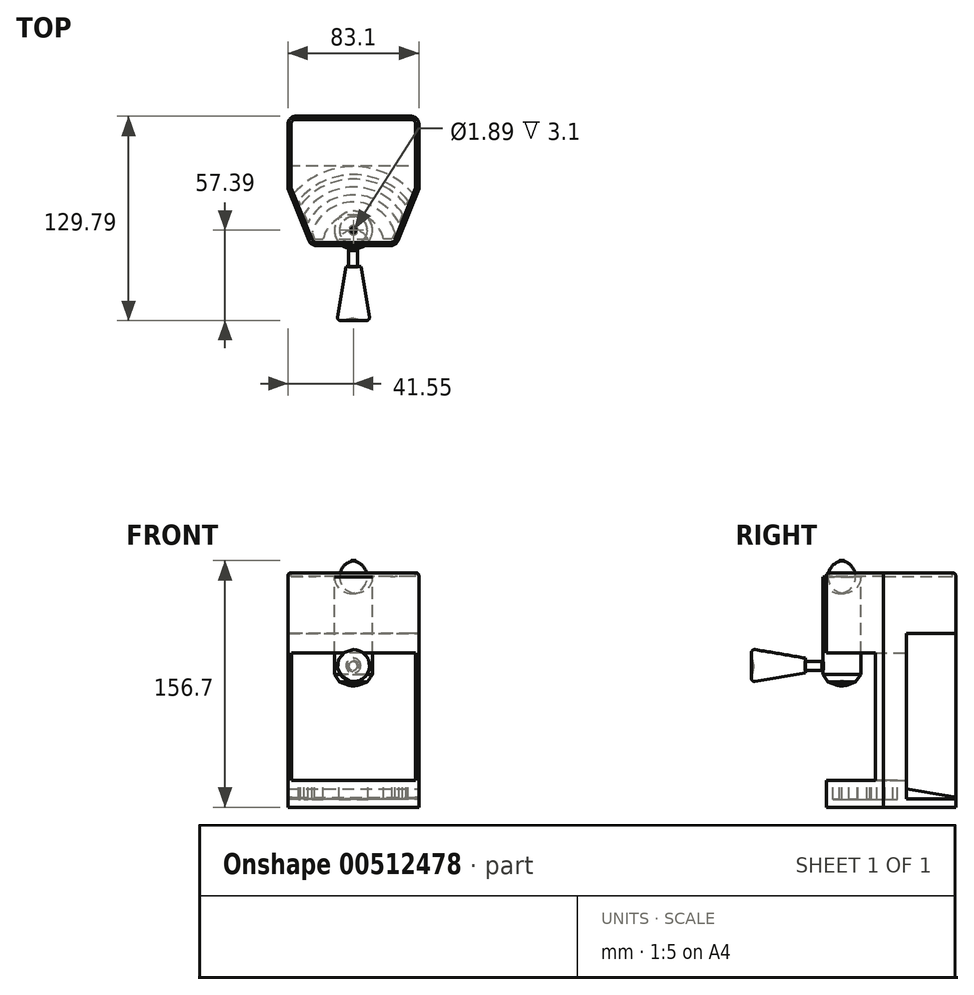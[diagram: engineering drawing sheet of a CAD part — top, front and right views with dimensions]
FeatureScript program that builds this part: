
annotation { "Feature Type Name" : "Feature", "Feature Type Description" : "" }
export const myFeature = defineFeature(function(context is Context, id is Id, definition is map)
    precondition{}
    {
        {
            var Q0;
            Q0=qCreatedBy(makeId("Top.planeOp"),FACE);
            var sketch = newSketch(context, id + "F0", { "sketchPlane" : qUnion([Q0])});
            skLineSegment(sketch, "E0.bottom", {"start": v(23.61, -41.08) * mm, "end": v(-23.61, -41.08) * mm});
            skLineSegment(sketch, "E0.top", {"start": v(36.55, 41.08) * mm, "end": v(-36.55, 41.08) * mm});
            skLineSegment(sketch, "E0.left", {"start": v(41.55, -4.86) * mm, "end": v(41.55, 36.08) * mm});
            skLineSegment(sketch, "E0.right", {"start": v(-41.55, -4.86) * mm, "end": v(-41.55, 36.08) * mm});
            skPoint(sketch, "E0.middle", {"position": v(0, 0) * mm});
            skLineSegment(sketch, "E1", {"start": v(-41.55, -4.86) * mm, "end": v(-28.25, -37.94) * mm});
            skPoint(sketch, "E2.orphan", {"position": v(-41.55, -41.08) * mm});
            skLineSegment(sketch, "E3.MirrorCS", {"start": v(41.55, -4.86) * mm, "end": v(28.25, -37.94) * mm});
            skPoint(sketch, "E4.orphan", {"position": v(41.55, -41.08) * mm});
            skPoint(sketch, "E5.orphan", {"position": v(-50.34, 17.01) * mm});
            skPoint(sketch, "E6.start.orphan", {"position": v(-21.47, -54.8) * mm});
            skPoint(sketch, "E7.orphan", {"position": v(21.47, -54.8) * mm});
            skPoint(sketch, "E8.orphan", {"position": v(50.34, 17.01) * mm});
            skPoint(sketch, "E9.visualSharp", {"position": v(-41.55, 41.08) * mm});
            skArc(sketch, "E9.filletArc", {"start": v(-36.55, 41.08) * mm, "mid": v(-40.08, 39.61) * mm, "end": v(-41.55, 36.08) * mm});
            skPoint(sketch, "E10.visualSharp", {"position": v(41.55, 41.08) * mm});
            skArc(sketch, "E10.filletArc", {"start": v(41.55, 36.08) * mm, "mid": v(40.08, 39.61) * mm, "end": v(36.55, 41.08) * mm});
            skPoint(sketch, "E11.visualSharp", {"position": v(-27, -41.08) * mm});
            skArc(sketch, "E11.filletArc", {"start": v(-28.25, -37.94) * mm, "mid": v(-26.41, -40.22) * mm, "end": v(-23.61, -41.08) * mm});
            skPoint(sketch, "E12.visualSharp", {"position": v(27, -41.08) * mm});
            skArc(sketch, "E12.filletArc", {"start": v(23.61, -41.08) * mm, "mid": v(26.41, -40.22) * mm, "end": v(28.25, -37.94) * mm});
            skSolve(sketch);
        }
        {
            var Q0;
            Q0=makeQuery(id+"F0.imprint","IMPRINT",FACE,{"disambiguationData":[TD([[makeQuery(id+"F0.imprint","IMPRINT",EDGE,{"derivedFrom":sQuery(id+"F0.wireOp",EDGE,"E0.bottom")}),-1.0]])]});
            extrude(context, id + "F1", {"entities" : qUnion([Q0]), "depth" : 149 * mm});
        }
        {
            var Q0;
            Q0=qCreatedBy(makeId("Top.planeOp"),FACE);
            cPlane(context, id + "F2", {"entities" : qUnion([Q0]), "cplaneType" : CPlaneType.OFFSET, "offset" : 17 * mm, "width" : 150 * mm, "height" : 150 * mm});
        }
        {
            var Q0;
            Q0=qCreatedBy(id+"F2.planeOp",FACE);
            var sketch = newSketch(context, id + "F3", { "sketchPlane" : qUnion([Q0])});
            skCircle(sketch, "E13", {"center": v(0, -41.15) * mm, "radius": 50.23 * mm});
            skSolve(sketch);
        }
        {
            var Q0;
            Q0=makeQuery(id+"F3.imprint","IMPRINT",FACE,{"disambiguationData":[TD([[makeQuery(id+"F3.imprint","IMPRINT",EDGE,{"derivedFrom":sQuery(id+"F3.wireOp",EDGE,"E13")}),1.0]])]});
            extrude(context, id + "F4", {"entities" : qUnion([Q0]), "operationType" : NewBodyOperationType.REMOVE, "depth" : 81 * mm});
        }
        {
            var Q0;
            Q0=makeQuery(id+"F4.boolean.opBoolean","COPY",FACE,{"derivedFrom":makeQuery(id+"F4.opExtrude","CAP_FACE",FACE,{"disambiguationData":[OSD([sQuery(id+"F3.wireOp",EDGE,"E13")])],"isStart":false})});
            cPlane(context, id + "F5", {"entities" : qUnion([Q0]), "cplaneType" : CPlaneType.OFFSET, "offset" : 0 * mm, "width" : 150 * mm, "height" : 150 * mm});
        }
        {
            var Q0;
            Q0=makeQuery(id+"F1.opExtrude","CAP_FACE",FACE,{"disambiguationData":[OSD([sQuery(id+"F0.wireOp",EDGE,"E0.bottom"),sQuery(id+"F0.wireOp",EDGE,"E0.top"),sQuery(id+"F0.wireOp",EDGE,"E0.left"),sQuery(id+"F0.wireOp",EDGE,"E0.right"),sQuery(id+"F0.wireOp",EDGE,"E1"),sQuery(id+"F0.wireOp",EDGE,"E3.MirrorCS"),sQuery(id+"F0.wireOp",EDGE,"E9.filletArc"),sQuery(id+"F0.wireOp",EDGE,"E10.filletArc"),sQuery(id+"F0.wireOp",EDGE,"E11.filletArc"),sQuery(id+"F0.wireOp",EDGE,"E12.filletArc")])],"isStart":false});
            fillet(context, id + "F6", {"entities" : qUnion([Q0]), "radius" : 2 * mm, "tangentPropagation" : true, "allowEdgeOverflow" : false});
        }
        {
            var Q0;
            Q0=qCreatedBy(id+"F5.planeOp",FACE);
            var sketch = newSketch(context, id + "F7", { "sketchPlane" : qUnion([Q0])});
            skCircle(sketch, "E14", {"center": v(0, 31.32) * mm, "radius": 12.05 * mm});
            skSolve(sketch);
        }
        {
            var Q0;
            Q0=makeQuery(id+"F1.opExtrude","CAP_FACE",FACE,{"disambiguationData":[OSD([sQuery(id+"F0.wireOp",EDGE,"E0.bottom"),sQuery(id+"F0.wireOp",EDGE,"E0.top"),sQuery(id+"F0.wireOp",EDGE,"E0.left"),sQuery(id+"F0.wireOp",EDGE,"E0.right"),sQuery(id+"F0.wireOp",EDGE,"E1"),sQuery(id+"F0.wireOp",EDGE,"E3.MirrorCS"),sQuery(id+"F0.wireOp",EDGE,"E9.filletArc"),sQuery(id+"F0.wireOp",EDGE,"E10.filletArc"),sQuery(id+"F0.wireOp",EDGE,"E11.filletArc"),sQuery(id+"F0.wireOp",EDGE,"E12.filletArc")])],"isStart":false});
            extrude(context, id + "F8", {"entities" : qUnion([Q0]), "operationType" : NewBodyOperationType.REMOVE, "oppositeDirection" : true, "depth" : 2.5 * mm, "offsetDistance" : 25 * mm});
        }
        {
            var Q0;
            Q0=makeQuery(id+"F7.imprint","IMPRINT",FACE,{"disambiguationData":[TD([[makeQuery(id+"F7.imprint","IMPRINT",EDGE,{"derivedFrom":sQuery(id+"F7.wireOp",EDGE,"E14")}),1.0]])]});
            extrude(context, id + "F9", {"entities" : qUnion([Q0]), "depth" : 20.8 * mm, "hasSecondDirection" : true, "secondDirectionOppositeDirection" : true, "secondDirectionDepth" : 58.7 * mm, "offsetDistance" : 25 * mm});
        }
        {
            var Q0;
            Q0=makeQuery(id+"F9.opExtrude","CAP_EDGE",EDGE,{"disambiguationData":[OSD([sQuery(id+"F7.wireOp",EDGE,"E14")])],"isStart":false});
            chamfer(context, id + "F10", {"entities" : qUnion([Q0]), "chamferType" : ChamferType.OFFSET_ANGLE, "width" : 10 * mm, "oppositeDirection" : false, "angle" : 20 * degree, "tangentPropagation" : true});
        }
        {
            var Q0;
            Q0=makeQuery(id+"F4.boolean.opBoolean","COPY",FACE,{"derivedFrom":makeQuery(id+"F4.opExtrude","CAP_FACE",FACE,{"disambiguationData":[OSD([sQuery(id+"F3.wireOp",EDGE,"E13")])],"isStart":true})});
            cPlane(context, id + "F11", {"entities" : qUnion([Q0]), "cplaneType" : CPlaneType.OFFSET, "offset" : 0 * mm, "width" : 150 * mm, "height" : 150 * mm});
        }
        {
            var Q0;
            Q0=qCreatedBy(id+"F11.planeOp",FACE);
            var sketch = newSketch(context, id + "F12", { "sketchPlane" : qUnion([Q0])});
            skArc(sketch, "E15", {"start": v(34.7, -12.42) * mm, "mid": v(0, 3.9) * mm, "end": v(-34.7, -12.42) * mm});
            skArc(sketch, "E16", {"start": v(33.47, -15.42) * mm, "mid": v(0, 1.06) * mm, "end": v(-33.47, -15.42) * mm});
            skArc(sketch, "E17", {"start": v(31.22, -20.93) * mm, "mid": v(0, -3.95) * mm, "end": v(-31.22, -20.93) * mm});
            skArc(sketch, "E18", {"start": v(28.85, -26.71) * mm, "mid": v(0, -8.89) * mm, "end": v(-28.85, -26.71) * mm});
            skArc(sketch, "E19", {"start": v(26.4, -32.73) * mm, "mid": v(0, -13.45) * mm, "end": v(-26.4, -32.73) * mm});
            skArc(sketch, "E20", {"start": v(19.24, -37.09) * mm, "mid": v(0, -21.49) * mm, "end": v(-19.24, -37.09) * mm});
            skArc(sketch, "E21", {"start": v(9.18, -37.09) * mm, "mid": v(0, -31.11) * mm, "end": v(-9.18, -37.09) * mm});
            skLineSegment(sketch, "E22", {"start": v(-34.7, -12.42) * mm, "end": v(-33.47, -15.42) * mm});
            skLineSegment(sketch, "E23", {"start": v(-24.6, -37.09) * mm, "end": v(-19.24, -37.09) * mm});
            skLineSegment(sketch, "E24.MirrorCS", {"start": v(24.6, -37.09) * mm, "end": v(19.24, -37.09) * mm});
            skLineSegment(sketch, "E25.MirrorCS", {"start": v(34.7, -12.42) * mm, "end": v(33.47, -15.42) * mm});
            skPoint(sketch, "E26.orphan", {"position": v(-38.23, -3.78) * mm});
            skPoint(sketch, "E27.orphan", {"position": v(38.23, -3.78) * mm});
            skLineSegment(sketch, "E28.trimOffspring", {"start": v(-31.22, -20.93) * mm, "end": v(-28.85, -26.71) * mm});
            skLineSegment(sketch, "E29.trimOffspring", {"start": v(31.22, -20.93) * mm, "end": v(28.85, -26.71) * mm});
            skLineSegment(sketch, "E30.trimOffspring", {"start": v(26.4, -32.73) * mm, "end": v(24.6, -37.09) * mm});
            skLineSegment(sketch, "E31.trimOffspring", {"start": v(-26.4, -32.73) * mm, "end": v(-24.6, -37.09) * mm});
            skPoint(sketch, "E32.trimOffspring.end.orphan", {"position": v(5.22, -37.09) * mm});
            skPoint(sketch, "E33.trimOffspring.end.orphan", {"position": v(-5.22, -37.09) * mm});
            skLineSegment(sketch, "E34", {"start": v(-9.18, -37.09) * mm, "end": v(9.18, -37.09) * mm});
            skSolve(sketch);
        }
        {
            var Q0;
            Q0=makeQuery(id+"F12.imprint","IMPRINT",FACE,{"disambiguationData":[TD([[makeQuery(id+"F12.imprint","IMPRINT",EDGE,{"derivedFrom":sQuery(id+"F12.wireOp",EDGE,"E19")}),1.0]])]});
            var Q1;
            Q1=makeQuery(id+"F12.imprint","IMPRINT",FACE,{"disambiguationData":[TD([[makeQuery(id+"F12.imprint","IMPRINT",EDGE,{"derivedFrom":sQuery(id+"F12.wireOp",EDGE,"E17")}),1.0]])]});
            var Q2;
            Q2=makeQuery(id+"F12.imprint","IMPRINT",FACE,{"disambiguationData":[TD([[makeQuery(id+"F12.imprint","IMPRINT",EDGE,{"derivedFrom":sQuery(id+"F12.wireOp",EDGE,"E15")}),1.0]])]});
            var Q3;
            Q3=makeQuery(id+"F12.imprint","IMPRINT",FACE,{"disambiguationData":[TD([[makeQuery(id+"F12.imprint","IMPRINT",EDGE,{"derivedFrom":sQuery(id+"F12.wireOp",EDGE,"E21")}),1.0]])]});
            extrude(context, id + "F13", {"entities" : qUnion([Q0, Q1, Q2, Q3]), "operationType" : NewBodyOperationType.REMOVE, "oppositeDirection" : true, "depth" : 11.9 * mm});
        }
        {
            var Q0;
            Q0=makeQuery(id+"F9.opExtrude","CAP_EDGE",EDGE,{"disambiguationData":[OSD([sQuery(id+"F7.wireOp",EDGE,"E14")])],"isStart":true});
            fillet(context, id + "F14", {"entities" : qUnion([Q0]), "radius" : 10.38 * mm, "tangentPropagation" : true, "allowEdgeOverflow" : false});
        }
        {
            var Q0;
            Q0=qCreatedBy(makeId("Right.planeOp"),FACE);
            var sketch = newSketch(context, id + "F15", { "sketchPlane" : qUnion([Q0])});
            skLineSegment(sketch, "E35", {"start": v(50.85, 137.76) * mm, "end": v(50.85, 110.55) * mm});
            skLineSegment(sketch, "E36", {"start": v(50.85, 110.55) * mm, "end": v(9.66, 110.55) * mm});
            skLineSegment(sketch, "E37", {"start": v(9.66, 110.55) * mm, "end": v(9.66, 11.61) * mm});
            skLineSegment(sketch, "E38", {"start": v(9.66, 11.61) * mm, "end": v(46.8, 5.36) * mm});
            skLineSegment(sketch, "E39", {"start": v(46.8, 5.36) * mm, "end": v(79.54, 105.4) * mm});
            skLineSegment(sketch, "E40", {"start": v(79.54, 105.4) * mm, "end": v(50.85, 137.76) * mm});
            skSolve(sketch);
        }
        {
            var Q0;
            Q0=makeQuery(id+"F15.imprint","IMPRINT",FACE,{"disambiguationData":[TD([[makeQuery(id+"F15.imprint","IMPRINT",EDGE,{"derivedFrom":sQuery(id+"F15.wireOp",EDGE,"E35")}),1.0]])]});
            extrude(context, id + "F16", {"entities" : qUnion([Q0]), "operationType" : NewBodyOperationType.REMOVE, "oppositeDirection" : true, "depth" : 88 * mm, "offsetDistance" : 25 * mm, "symmetric" : true});
        }
        {
            var Q0;
            Q0=makeQuery(id+"F16.boolean.opBoolean","COPY",FACE,{"derivedFrom":makeQuery(id+"F16.opExtrude","SWEPT_FACE",FACE,{"disambiguationData":[OSD([sQuery(id+"F15.wireOp",EDGE,"E36")])]})});
            extrude(context, id + "F17", {"entities" : qUnion([Q0]), "depth" : 105.3 * mm, "offsetDistance" : 25 * mm});
        }
        {
            var Q0;
            {var subQ2=sQuery(id+"F0.wireOp",EDGE,"E0.bottom");Q0=makeQuery(id+"F4.boolean.opBoolean","SPLIT",FACE,{"disambiguationData":[TD([makeQuery(id+"F4.opExtrude","CAP_FACE",FACE,{"disambiguationData":[OSD([sQuery(id+"F3.wireOp",EDGE,"E13")])],"isStart":false})])],"derivedFrom":makeQuery(id+"F1.opExtrude","SWEPT_FACE",FACE,{"disambiguationData":[OSD([subQ2])]})});}
            var sketch = newSketch(context, id + "F18", { "sketchPlane" : qUnion([Q0])});
            skCircle(sketch, "E41", {"center": v(-0.2, 89.77) * mm, "radius": 2.75 * mm});
            skSolve(sketch);
        }
        {
            var Q0;
            Q0 = qSketchRegion(id + "F18", true);
            extrude(context, id + "F19", {"entities" : qUnion([Q0]), "operationType" : NewBodyOperationType.ADD, "depth" : 14 * mm, "offsetDistance" : 25 * mm});
        }
        {
            var Q0;
            Q0=qCreatedBy(makeId("Right.planeOp"),FACE);
            var sketch = newSketch(context, id + "F20", { "sketchPlane" : qUnion([Q0])});
            skLineSegment(sketch, "E42", {"start": v(-55, 90.05) * mm, "end": v(-87.25, 90.05) * mm});
            skLineSegment(sketch, "E43", {"start": v(-87.25, 90.05) * mm, "end": v(-88.68, 97.87) * mm});
            skLineSegment(sketch, "E44", {"start": v(-86.37, 100.2) * mm, "end": v(-54.55, 94.74) * mm});
            skLineSegment(sketch, "E45", {"start": v(-54.55, 94.74) * mm, "end": v(-55, 90.05) * mm});
            skPoint(sketch, "E46.visualSharp", {"position": v(-89.19, 100.69) * mm});
            skArc(sketch, "E46.filletArc", {"start": v(-86.37, 100.2) * mm, "mid": v(-88.13, 99.64) * mm, "end": v(-88.68, 97.87) * mm});
            skSolve(sketch);
        }
        {
            var Q0;
            Q0=makeQuery(id+"F20.imprint","IMPRINT",FACE,{"disambiguationData":[TD([[makeQuery(id+"F20.imprint","IMPRINT",EDGE,{"derivedFrom":sQuery(id+"F20.wireOp",EDGE,"E42")}),-1.0]])]});
            var Q1;
            Q1=sQuery(id+"F20.wireOp",EDGE,"E42");
            revolve(context, id + "F21", {"entities" : qUnion([Q0]), "axis" : qUnion([Q1]), "revolveType" : RevolveType.FULL});
        }
        {
            var Q0;
            Q0=makeQuery(id+"F9.opExtrude","CAP_FACE",FACE,{"disambiguationData":[OSD([sQuery(id+"F7.wireOp",EDGE,"E14")])],"isStart":false});
            var sketch = newSketch(context, id + "F22", { "sketchPlane" : qUnion([Q0])});
            skCircle(sketch, "E47", {"center": v(0, 31.32) * mm, "radius": 0.94 * mm});
            skSolve(sketch);
        }
        {
            var Q0;
            Q0=makeQuery(id+"F22.imprint","IMPRINT",FACE,{"disambiguationData":[TD([[makeQuery(id+"F22.imprint","IMPRINT",EDGE,{"derivedFrom":sQuery(id+"F22.wireOp",EDGE,"E47")}),1.0]])]});
            extrude(context, id + "F23", {"entities" : qUnion([Q0]), "operationType" : NewBodyOperationType.REMOVE, "oppositeDirection" : true, "depth" : 3.1 * mm, "offsetDistance" : 25 * mm});
        }
        {
            var Q0;
            Q0=makeQuery(id+"F10.opChamfer","BLEND_FACE",FACE,{"disambiguationData":[OSD([sQuery(id+"F7.wireOp",EDGE,"E14")])]});
            chamfer(context, id + "F24", {"entities" : qUnion([Q0]), "width" : 5 * mm, "tangentPropagation" : true});
        }
        {
            var Q0;
            Q0=makeQuery(id+"F19.boolean.opBoolean","INTERSECT",EDGE,{"derivedFrom":[makeQuery(id+"F9.opExtrude","SWEPT_FACE",FACE,{"disambiguationData":[OSD([sQuery(id+"F7.wireOp",EDGE,"E14")])]}),makeQuery(id+"F19.opExtrude","SWEPT_FACE",FACE,{"disambiguationData":[OSD([sQuery(id+"F18.wireOp",EDGE,"E41")])]})]});
            fillet(context, id + "F25", {"entities" : qUnion([Q0]), "radius" : 1 * mm, "tangentPropagation" : true, "allowEdgeOverflow" : false});
        }
    });
